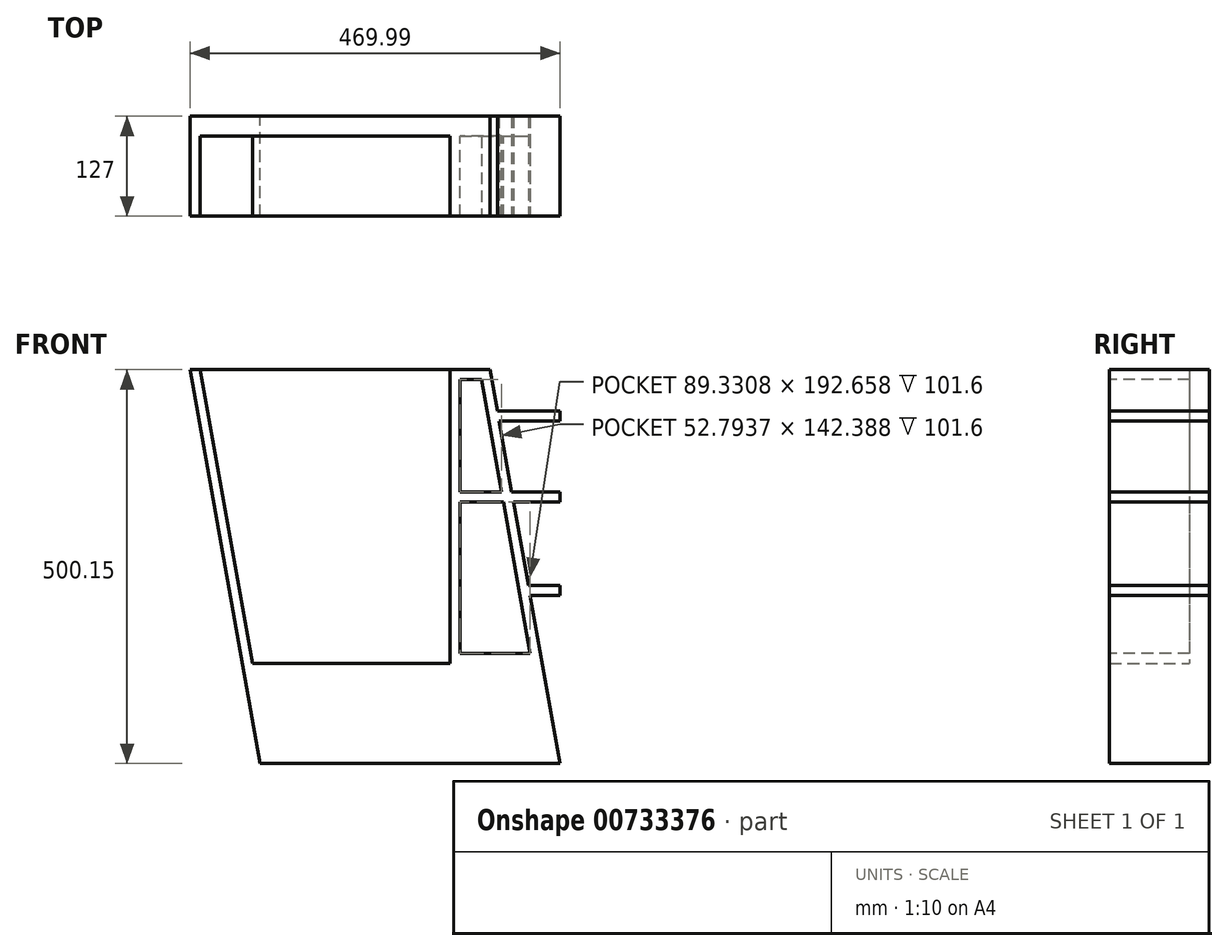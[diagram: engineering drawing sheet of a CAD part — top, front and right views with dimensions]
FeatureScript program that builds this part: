
annotation { "Feature Type Name" : "Feature", "Feature Type Description" : "" }
export const myFeature = defineFeature(function(context is Context, id is Id, definition is map)
    precondition{}
    {
        {
            var Q0;
            Q0=qCreatedBy(makeId("Front.planeOp"),FACE);
            var sketch = newSketch(context, id + "F0", { "sketchPlane" : qUnion([Q0])});
            skLineSegment(sketch, "E0", {"start": v(0, 0) * mm, "end": v(381, 0) * mm});
            skLineSegment(sketch, "E1", {"start": v(-88.99, 500.15) * mm, "end": v(292.01, 500.15) * mm});
            skLineSegment(sketch, "E2", {"start": v(-88.99, 500.15) * mm, "end": v(0, 0) * mm});
            skLineSegment(sketch, "E3", {"start": v(292.01, 500.15) * mm, "end": v(381, 0) * mm});
            skSolve(sketch);
        }
        {
            var Q0;
            Q0=makeQuery(id+"F0.imprint","IMPRINT",FACE,{"disambiguationData":[TD([[makeQuery(id+"F0.imprint","IMPRINT",EDGE,{"derivedFrom":sQuery(id+"F0.wireOp",EDGE,"E0")}),1.0]])]});
            extrude(context, id + "F1", {"entities" : qUnion([Q0]), "depth" : 25.4 * mm, "offsetDistance" : 25.4 * mm});
        }
        {
            var Q0;
            Q0=makeQuery(id+"F1.opExtrude","CAP_FACE",FACE,{"disambiguationData":[OSD([sQuery(id+"F0.wireOp",EDGE,"E0"),sQuery(id+"F0.wireOp",EDGE,"E1"),sQuery(id+"F0.wireOp",EDGE,"E2"),sQuery(id+"F0.wireOp",EDGE,"E3")])],"isStart":false});
            var sketch = newSketch(context, id + "F2", { "sketchPlane" : qUnion([Q0])});
            skLineSegment(sketch, "E4", {"start": v(0, 0) * mm, "end": v(381, 0) * mm});
            skLineSegment(sketch, "E5", {"start": v(381, 0) * mm, "end": v(358.4, 127) * mm});
            skLineSegment(sketch, "E6", {"start": v(358.4, 127) * mm, "end": v(-22.6, 127) * mm});
            skLineSegment(sketch, "E7", {"start": v(-22.6, 127) * mm, "end": v(0, 0) * mm});
            skSolve(sketch);
        }
        {
            var Q0;
            Q0=makeQuery(id+"F2.imprint","IMPRINT",FACE,{"disambiguationData":[TD([[makeQuery(id+"F2.imprint","IMPRINT",EDGE,{"derivedFrom":sQuery(id+"F2.wireOp",EDGE,"E4")}),1.0]])]});
            extrude(context, id + "F3", {"entities" : qUnion([Q0]), "operationType" : NewBodyOperationType.ADD, "depth" : 101.6 * mm, "offsetDistance" : 25.4 * mm});
        }
        {
            var Q0;
            Q0=makeQuery(id+"F1.opExtrude","CAP_FACE",FACE,{"disambiguationData":[OSD([sQuery(id+"F0.wireOp",EDGE,"E0"),sQuery(id+"F0.wireOp",EDGE,"E1"),sQuery(id+"F0.wireOp",EDGE,"E2"),sQuery(id+"F0.wireOp",EDGE,"E3")])],"isStart":false});
            var sketch = newSketch(context, id + "F4", { "sketchPlane" : qUnion([Q0])});
            skLineSegment(sketch, "E8", {"start": v(241.21, 500.15) * mm, "end": v(241.21, 127) * mm});
            skSolve(sketch);
        }
        {
            var Q0;
            {var subQ0=sQuery(id+"F4.wireOp",EDGE,"E8");Q0=makeQuery(id+"F4.imprint","IMPRINT",FACE,{"disambiguationData":[TD([[makeQuery(id+"F4.imprint","IMPRINT",EDGE,{"derivedFrom":subQ0}),1.0]])]});}
            extrude(context, id + "F5", {"entities" : qUnion([Q0]), "operationType" : NewBodyOperationType.ADD, "depth" : 101.6 * mm, "offsetDistance" : 25.4 * mm});
        }
        {
            var Q0;
            {var subQ0=sQuery(id+"F2.wireOp",EDGE,"E6");Q0=makeQuery(id+"F5.boolean.opBoolean","MERGE",FACE,{"derivedFrom":[makeQuery(id+"F3.opExtrude","CAP_FACE",FACE,{"disambiguationData":[OSD([sQuery(id+"F2.wireOp",EDGE,"E4"),sQuery(id+"F2.wireOp",EDGE,"E5"),subQ0,sQuery(id+"F2.wireOp",EDGE,"E7")])],"isStart":false}),makeQuery(id+"F5.opExtrude","CAP_FACE",FACE,{"disambiguationData":[OSD([sQuery(id+"F0.wireOp",EDGE,"E1"),sQuery(id+"F0.wireOp",EDGE,"E3"),subQ0,sQuery(id+"F4.wireOp",EDGE,"E8")])],"isStart":false})]});}
            var sketch = newSketch(context, id + "F6", { "sketchPlane" : qUnion([Q0])});
            skLineSegment(sketch, "E9", {"start": v(253.91, 487.45) * mm, "end": v(281.37, 487.45) * mm});
            skLineSegment(sketch, "E10", {"start": v(281.37, 487.45) * mm, "end": v(343.25, 139.7) * mm});
            skLineSegment(sketch, "E11", {"start": v(253.91, 487.45) * mm, "end": v(253.91, 139.7) * mm});
            skLineSegment(sketch, "E12", {"start": v(253.91, 139.7) * mm, "end": v(343.25, 139.7) * mm});
            skSolve(sketch);
        }
        {
            var Q0;
            Q0=makeQuery(id+"F6.imprint","IMPRINT",FACE,{"disambiguationData":[TD([[makeQuery(id+"F6.imprint","IMPRINT",EDGE,{"derivedFrom":sQuery(id+"F6.wireOp",EDGE,"E9")}),-1.0]])]});
            extrude(context, id + "F7", {"entities" : qUnion([Q0]), "operationType" : NewBodyOperationType.REMOVE, "oppositeDirection" : true, "depth" : 101.6 * mm, "offsetDistance" : 25.4 * mm});
        }
        {
            var Q0;
            {var subQ0=sQuery(id+"F2.wireOp",EDGE,"E6");Q0=makeQuery(id+"F5.boolean.opBoolean","MERGE",FACE,{"derivedFrom":[makeQuery(id+"F3.opExtrude","CAP_FACE",FACE,{"disambiguationData":[OSD([sQuery(id+"F2.wireOp",EDGE,"E4"),sQuery(id+"F2.wireOp",EDGE,"E5"),subQ0,sQuery(id+"F2.wireOp",EDGE,"E7")])],"isStart":false}),makeQuery(id+"F5.opExtrude","CAP_FACE",FACE,{"disambiguationData":[OSD([sQuery(id+"F0.wireOp",EDGE,"E1"),sQuery(id+"F0.wireOp",EDGE,"E3"),subQ0,sQuery(id+"F4.wireOp",EDGE,"E8")])],"isStart":false})]});}
            var sketch = newSketch(context, id + "F8", { "sketchPlane" : qUnion([Q0])});
            skLineSegment(sketch, "E13", {"start": v(381, 213.4) * mm, "end": v(381, 226.1) * mm});
            skLineSegment(sketch, "E14", {"start": v(303.66, 434.71) * mm, "end": v(381, 434.71) * mm});
            skLineSegment(sketch, "E15", {"start": v(321.87, 332.36) * mm, "end": v(381, 332.36) * mm});
            skLineSegment(sketch, "E16", {"start": v(343.03, 213.4) * mm, "end": v(381, 213.4) * mm});
            skLineSegment(sketch, "E17", {"start": v(301.4, 447.41) * mm, "end": v(381, 447.41) * mm});
            skLineSegment(sketch, "E18", {"start": v(319.6, 345.06) * mm, "end": v(381, 345.06) * mm});
            skLineSegment(sketch, "E19", {"start": v(340.77, 226.1) * mm, "end": v(381, 226.1) * mm});
            skPoint(sketch, "E20.orphan", {"position": v(381, 500.15) * mm});
            skLineSegment(sketch, "E21.trimOffspring", {"start": v(381, 434.71) * mm, "end": v(381, 447.41) * mm});
            skLineSegment(sketch, "E22.trimOffspring", {"start": v(381, 332.36) * mm, "end": v(381, 345.06) * mm});
            skSolve(sketch);
        }
        {
            var Q0;
            {var subQ0=sQuery(id+"F8.wireOp",EDGE,"E14");Q0=makeQuery(id+"F8.imprint","IMPRINT",FACE,{"disambiguationData":[TD([[makeQuery(id+"F8.imprint","IMPRINT",EDGE,{"derivedFrom":subQ0}),1.0]])]});}
            var Q1;
            {var subQ0=sQuery(id+"F8.wireOp",EDGE,"E15");Q1=makeQuery(id+"F8.imprint","IMPRINT",FACE,{"disambiguationData":[TD([[makeQuery(id+"F8.imprint","IMPRINT",EDGE,{"derivedFrom":subQ0}),1.0]])]});}
            var Q2;
            Q2=makeQuery(id+"F8.imprint","IMPRINT",FACE,{"disambiguationData":[TD([[makeQuery(id+"F8.imprint","IMPRINT",EDGE,{"derivedFrom":sQuery(id+"F8.wireOp",EDGE,"E13")}),1.0]])]});
            extrude(context, id + "F9", {"entities" : qUnion([Q0, Q1, Q2]), "operationType" : NewBodyOperationType.ADD, "oppositeDirection" : true, "depth" : 127 * mm, "offsetDistance" : 25.4 * mm});
        }
        {
            var Q0;
            Q0=makeQuery(id+"F7.boolean.opBoolean","COPY",FACE,{"derivedFrom":makeQuery(id+"F7.opExtrude","CAP_FACE",FACE,{"disambiguationData":[OSD([sQuery(id+"F6.wireOp",EDGE,"E9"),sQuery(id+"F6.wireOp",EDGE,"E10"),sQuery(id+"F6.wireOp",EDGE,"E11"),sQuery(id+"F6.wireOp",EDGE,"E12")])],"isStart":false})});
            var sketch = newSketch(context, id + "F10", { "sketchPlane" : qUnion([Q0])});
            skLineSegment(sketch, "E23", {"start": v(306.7, 345.06) * mm, "end": v(253.91, 345.06) * mm});
            skLineSegment(sketch, "E24", {"start": v(253.91, 345.06) * mm, "end": v(253.91, 332.36) * mm});
            skLineSegment(sketch, "E25", {"start": v(253.91, 332.36) * mm, "end": v(308.97, 332.36) * mm});
            skSolve(sketch);
        }
        {
            var Q0;
            {var subQ0=sQuery(id+"F10.wireOp",EDGE,"E23");Q0=makeQuery(id+"F10.imprint","IMPRINT",FACE,{"disambiguationData":[TD([[makeQuery(id+"F10.imprint","IMPRINT",EDGE,{"derivedFrom":subQ0}),1.0]])]});}
            extrude(context, id + "F11", {"entities" : qUnion([Q0]), "operationType" : NewBodyOperationType.ADD, "depth" : 101.6 * mm, "offsetDistance" : 25.4 * mm});
        }
        {
            var Q0;
            Q0=makeQuery(id+"F1.opExtrude","CAP_FACE",FACE,{"disambiguationData":[OSD([sQuery(id+"F0.wireOp",EDGE,"E0"),sQuery(id+"F0.wireOp",EDGE,"E1"),sQuery(id+"F0.wireOp",EDGE,"E2"),sQuery(id+"F0.wireOp",EDGE,"E3")])],"isStart":false});
            var sketch = newSketch(context, id + "F12", { "sketchPlane" : qUnion([Q0])});
            skLineSegment(sketch, "E26", {"start": v(-76.09, 500.15) * mm, "end": v(-9.7, 127) * mm});
            skSolve(sketch);
        }
        {
            var Q0;
            {var subQ0=sQuery(id+"F12.wireOp",EDGE,"E26");Q0=makeQuery(id+"F12.imprint","IMPRINT",FACE,{"disambiguationData":[TD([[makeQuery(id+"F12.imprint","IMPRINT",EDGE,{"derivedFrom":subQ0}),-1.0]])]});}
            extrude(context, id + "F13", {"entities" : qUnion([Q0]), "operationType" : NewBodyOperationType.ADD, "depth" : 101.6 * mm, "offsetDistance" : 25.4 * mm});
        }
    });
